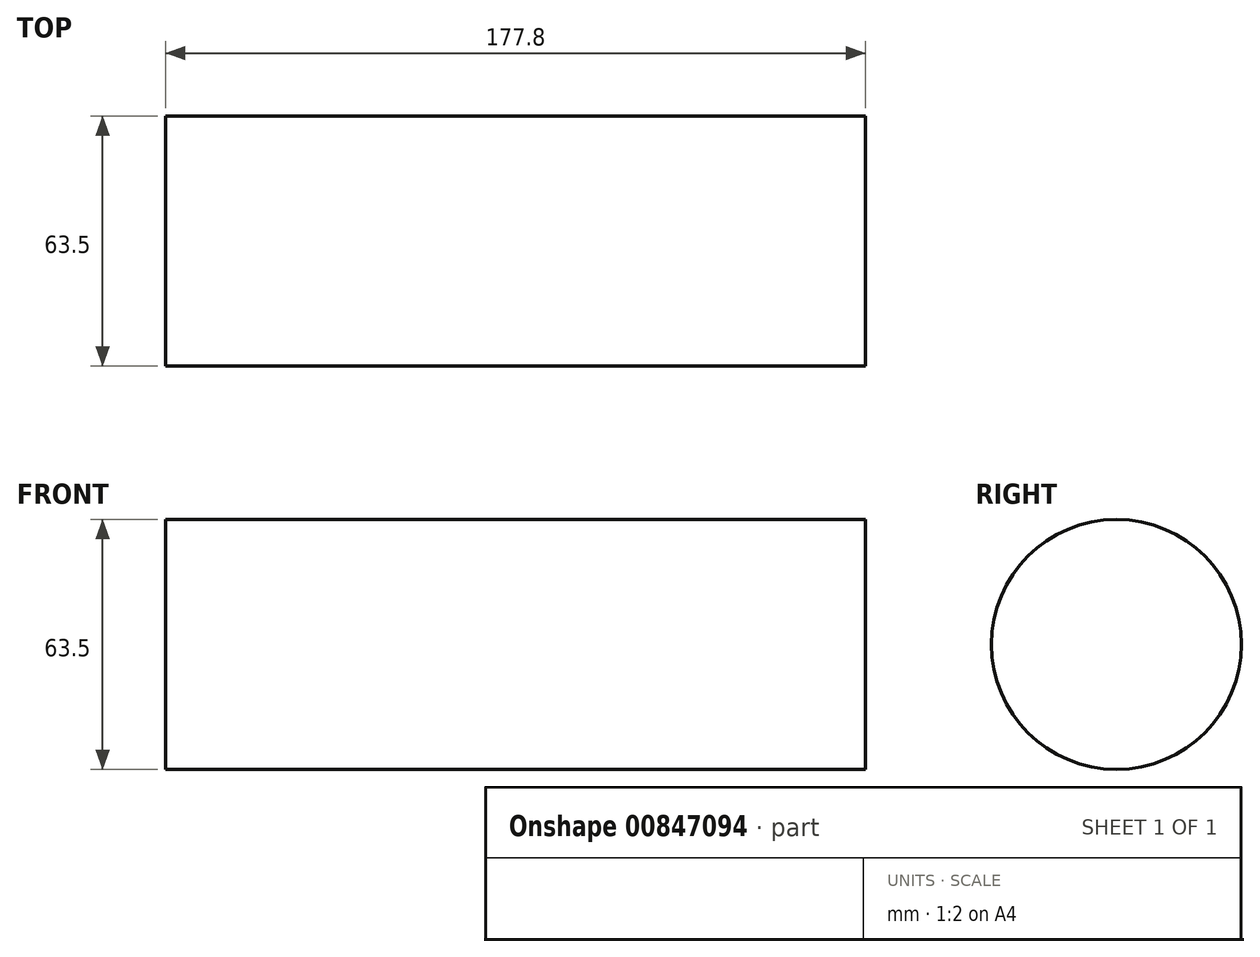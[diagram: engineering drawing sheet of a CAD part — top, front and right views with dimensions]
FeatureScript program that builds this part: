
annotation { "Feature Type Name" : "Feature", "Feature Type Description" : "" }
export const myFeature = defineFeature(function(context is Context, id is Id, definition is map)
    precondition{}
    {
        {
            var Q0;
            Q0=qCreatedBy(makeId("Right.planeOp"),FACE);
            var sketch = newSketch(context, id + "F0", { "sketchPlane" : qUnion([Q0])});
            skCircle(sketch, "E0", {"center": v(0, 0) * mm, "radius": 31.75 * mm});
            skSolve(sketch);
        }
        {
            var Q0;
            Q0=makeQuery(id+"F0.imprint","IMPRINT",FACE,{"disambiguationData":[TD([[makeQuery(id+"F0.imprint","IMPRINT",EDGE,{"derivedFrom":sQuery(id+"F0.wireOp",EDGE,"E0")}),1.0]])]});
            extrude(context, id + "F1", {"entities" : qUnion([Q0]), "depth" : 177.8 * mm, "offsetDistance" : 25.4 * mm});
        }
    });
